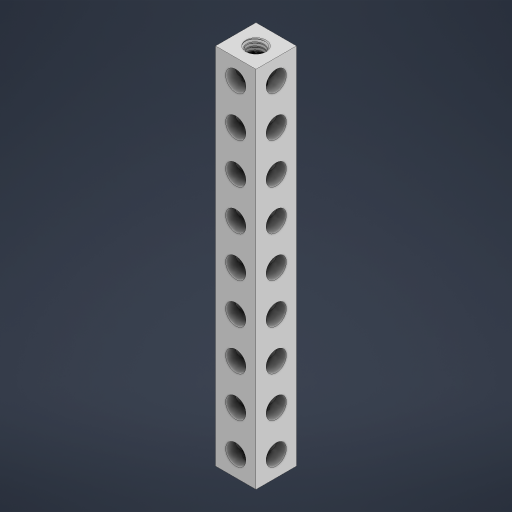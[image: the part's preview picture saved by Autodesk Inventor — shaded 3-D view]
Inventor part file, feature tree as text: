
AUTODESK INVENTOR PART (.ipt)
format: ipt  version: 2023 (Build 270158000, 158)  size: 1,338,368 bytes
history: native  units: in
note: dims shown in document units (in); Inventor stores cm internally (conversion verified against a paired STEP export)
features: mirror x1
ambient origin geometry x8: Origin, YZ Plane, XZ Plane, XY Plane, X Axis, Y Axis, Z Axis, Center Point
bodies: Solid1 (feature_tree)
feature tree (1):
  mirror  "Mirror3"
